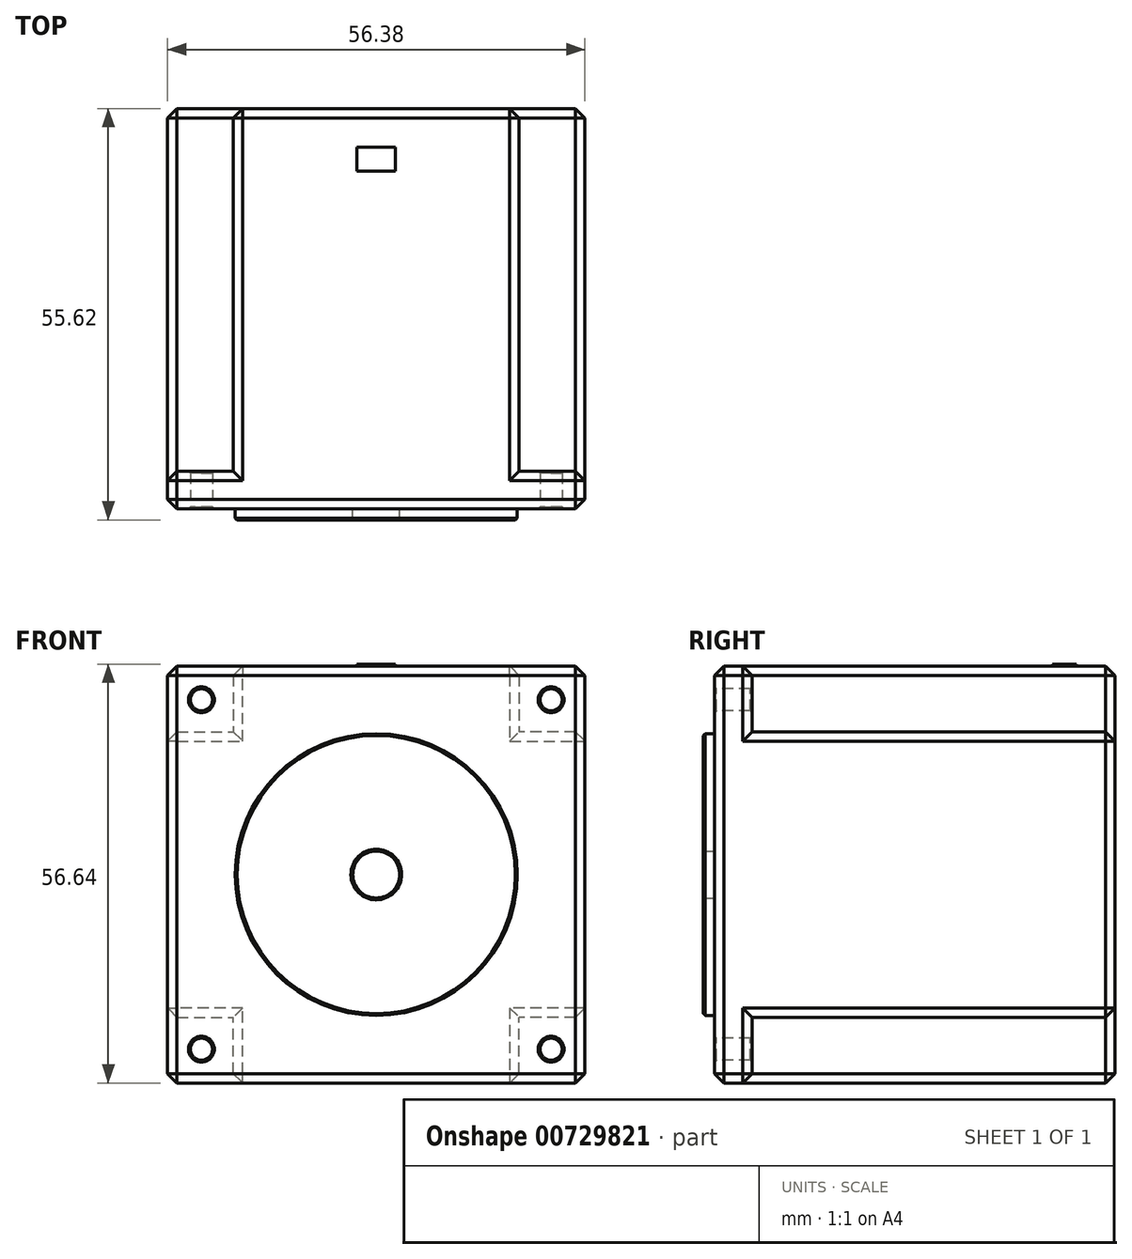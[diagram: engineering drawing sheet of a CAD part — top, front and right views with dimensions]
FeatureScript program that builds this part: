
annotation { "Feature Type Name" : "Feature", "Feature Type Description" : "" }
export const myFeature = defineFeature(function(context is Context, id is Id, definition is map)
    precondition{}
    {
        {
            var Q0;
            Q0=qCreatedBy(makeId("Front.planeOp"),FACE);
            var sketch = newSketch(context, id + "F0", { "sketchPlane" : qUnion([Q0])});
            skCircle(sketch, "E0", {"center": v(0, 0) * mm, "radius": 19.05 * mm});
            skLineSegment(sketch, "E1.bottom", {"start": v(28.2, 28.2) * mm, "end": v(-28.2, 28.2) * mm});
            skLineSegment(sketch, "E1.top", {"start": v(28.2, -28.2) * mm, "end": v(-28.2, -28.2) * mm});
            skLineSegment(sketch, "E1.left", {"start": v(28.2, 28.2) * mm, "end": v(28.2, -28.2) * mm});
            skLineSegment(sketch, "E1.right", {"start": v(-28.2, 28.2) * mm, "end": v(-28.2, -28.2) * mm});
            skCircle(sketch, "E2", {"center": v(0, 0) * mm, "radius": 3.18 * mm});
            skCircle(sketch, "E3", {"center": v(-23.62, 23.62) * mm, "radius": 1.49 * mm});
            skCircle(sketch, "E4", {"center": v(23.62, 23.62) * mm, "radius": 1.49 * mm});
            skCircle(sketch, "E5", {"center": v(23.62, -23.62) * mm, "radius": 1.49 * mm});
            skCircle(sketch, "E6", {"center": v(-23.62, -23.62) * mm, "radius": 1.49 * mm});
            skLineSegment(sketch, "E7", {"start": v(-23.62, 23.62) * mm, "end": v(-23.62, 28.2) * mm, "construction": true});
            skLineSegment(sketch, "E8", {"start": v(-23.62, 28.2) * mm, "end": v(-23.62, 23.62) * mm, "construction": true});
            skLineSegment(sketch, "E9", {"start": v(-23.62, 23.62) * mm, "end": v(-28.2, 23.62) * mm, "construction": true});
            skLineSegment(sketch, "E10", {"start": v(23.62, 23.62) * mm, "end": v(23.62, 28.2) * mm, "construction": true});
            skLineSegment(sketch, "E11", {"start": v(23.62, 23.62) * mm, "end": v(28.2, 23.62) * mm, "construction": true});
            skLineSegment(sketch, "E12", {"start": v(23.62, -23.62) * mm, "end": v(28.2, -23.62) * mm, "construction": true});
            skLineSegment(sketch, "E13", {"start": v(23.62, -23.62) * mm, "end": v(23.62, -28.2) * mm, "construction": true});
            skLineSegment(sketch, "E14", {"start": v(-23.62, -23.62) * mm, "end": v(-23.62, -28.2) * mm, "construction": true});
            skLineSegment(sketch, "E15", {"start": v(-23.62, -23.62) * mm, "end": v(-28.2, -23.62) * mm, "construction": true});
            skSolve(sketch);
        }
        {
            var Q0;
            Q0=qSketchRegion(id+"F0",true);
            var Q1;
            Q1=makeQuery(id+"F0.imprint","IMPRINT",FACE,{"disambiguationData":[TD([[makeQuery(id+"F0.imprint","IMPRINT",EDGE,{"derivedFrom":sQuery(id+"F0.wireOp",EDGE,"E0")}),1.0]])]});
            var Q2;
            Q2=makeQuery(id+"F0.imprint","IMPRINT",FACE,{"disambiguationData":[TD([[makeQuery(id+"F0.imprint","IMPRINT",EDGE,{"derivedFrom":sQuery(id+"F0.wireOp",EDGE,"E2")}),1.0]])]});
            extrude(context, id + "F1", {"entities" : qUnion([Q0, Q1, Q2]), "oppositeDirection" : true, "depth" : 54.1 * mm});
        }
        {
            var Q0;
            Q0=makeQuery(id+"F0.imprint","IMPRINT",FACE,{"disambiguationData":[TD([[makeQuery(id+"F0.imprint","IMPRINT",EDGE,{"derivedFrom":sQuery(id+"F0.wireOp",EDGE,"E0")}),1.0]])]});
            extrude(context, id + "F2", {"entities" : qUnion([Q0]), "operationType" : NewBodyOperationType.ADD, "depth" : 1.52 * mm});
        }
        {
            var Q0;
            Q0=makeQuery(id+"F0.imprint","IMPRINT",FACE,{"disambiguationData":[TD([[makeQuery(id+"F0.imprint","IMPRINT",EDGE,{"derivedFrom":sQuery(id+"F0.wireOp",EDGE,"E2")}),1.0]])]});
            extrude(context, id + "F3", {"entities" : qUnion([Q0]), "depth" : 20.32 * mm});
        }
        {
            var Q0;
            Q0=makeQuery(id+"F3.opExtrude","CAP_FACE",FACE,{"disambiguationData":[OSD([sQuery(id+"F0.wireOp",EDGE,"E2")])],"isStart":false});
            var sketch = newSketch(context, id + "F4", { "sketchPlane" : qUnion([Q0])});
            skLineSegment(sketch, "E16", {"start": v(-1.8, 2.62) * mm, "end": v(1.8, 2.62) * mm});
            skSolve(sketch);
        }
        {
            var Q0;
            {var subQ0=sQuery(id+"F4.wireOp",EDGE,"E16");Q0=makeQuery(id+"F4.imprint","IMPRINT",FACE,{"disambiguationData":[TD([[makeQuery(id+"F4.imprint","IMPRINT",EDGE,{"derivedFrom":subQ0}),1.0]])]});}
            extrude(context, id + "F5", {"entities" : qUnion([Q0]), "operationType" : NewBodyOperationType.REMOVE, "oppositeDirection" : true, "depth" : 12.7 * mm});
        }
        {
            var Q0;
            Q0=makeQuery(id+"F1.opExtrude","CAP_FACE",FACE,{"disambiguationData":[OSD([sQuery(id+"F0.wireOp",EDGE,"E1.bottom"),sQuery(id+"F0.wireOp",EDGE,"E1.top"),sQuery(id+"F0.wireOp",EDGE,"E1.left"),sQuery(id+"F0.wireOp",EDGE,"E1.right"),sQuery(id+"F0.wireOp",EDGE,"E3"),sQuery(id+"F0.wireOp",EDGE,"E4"),sQuery(id+"F0.wireOp",EDGE,"E5"),sQuery(id+"F0.wireOp",EDGE,"E6")])],"isStart":false});
            var sketch = newSketch(context, id + "F6", { "sketchPlane" : qUnion([Q0])});
            skLineSegment(sketch, "E17.bottom", {"start": v(-28.2, 28.2) * mm, "end": v(-19.3, 28.2) * mm});
            skLineSegment(sketch, "E17.top", {"start": v(-28.2, 19.3) * mm, "end": v(-19.3, 19.3) * mm});
            skLineSegment(sketch, "E17.left", {"start": v(-28.2, 28.2) * mm, "end": v(-28.2, 19.3) * mm});
            skLineSegment(sketch, "E17.right", {"start": v(-19.3, 28.2) * mm, "end": v(-19.3, 19.3) * mm});
            skLineSegment(sketch, "E18.bottom", {"start": v(28.2, 28.2) * mm, "end": v(19.3, 28.2) * mm});
            skLineSegment(sketch, "E18.top", {"start": v(28.2, 19.3) * mm, "end": v(19.3, 19.3) * mm});
            skLineSegment(sketch, "E18.left", {"start": v(28.2, 28.2) * mm, "end": v(28.2, 19.3) * mm});
            skLineSegment(sketch, "E18.right", {"start": v(19.3, 28.2) * mm, "end": v(19.3, 19.3) * mm});
            skLineSegment(sketch, "E19.bottom", {"start": v(28.2, -28.2) * mm, "end": v(19.3, -28.2) * mm});
            skLineSegment(sketch, "E19.top", {"start": v(28.2, -19.3) * mm, "end": v(19.3, -19.3) * mm});
            skLineSegment(sketch, "E19.left", {"start": v(28.2, -28.2) * mm, "end": v(28.2, -19.3) * mm});
            skLineSegment(sketch, "E19.right", {"start": v(19.3, -28.2) * mm, "end": v(19.3, -19.3) * mm});
            skLineSegment(sketch, "E20.bottom", {"start": v(-28.2, -28.2) * mm, "end": v(-19.3, -28.2) * mm});
            skLineSegment(sketch, "E20.top", {"start": v(-28.2, -19.3) * mm, "end": v(-19.3, -19.3) * mm});
            skLineSegment(sketch, "E20.left", {"start": v(-28.2, -28.2) * mm, "end": v(-28.2, -19.3) * mm});
            skLineSegment(sketch, "E20.right", {"start": v(-19.3, -28.2) * mm, "end": v(-19.3, -19.3) * mm});
            skSolve(sketch);
        }
        {
            var Q0;
            Q0=qSketchRegion(id+"F6",true);
            var Q1;
            {var subQ0=sQuery(id+"F0.wireOp",EDGE,"E1.right");var subQ1=sQuery(id+"F0.wireOp",EDGE,"E1.left");var subQ2=sQuery(id+"F0.wireOp",EDGE,"E1.top");var subQ3=sQuery(id+"F0.wireOp",EDGE,"E1.bottom");var subQ4=sQuery(id+"F0.wireOp",EDGE,"E3");var subQ5=sQuery(id+"F0.wireOp",EDGE,"E4");var subQ6=sQuery(id+"F0.wireOp",EDGE,"E5");var subQ7=sQuery(id+"F0.wireOp",EDGE,"E6");Q1=makeQuery(id+"F2.boolean.opBoolean","SPLIT",FACE,{"disambiguationData":[TD([makeQuery(id+"F1.opExtrude","SWEPT_FACE",FACE,{"disambiguationData":[OSD([subQ3])]})])],"derivedFrom":makeQuery(id+"F1.opExtrude","CAP_FACE",FACE,{"disambiguationData":[OSD([subQ3,subQ2,subQ1,subQ0,subQ4,subQ5,subQ6,subQ7])],"isStart":true})});}
            extrude(context, id + "F7", {"entities" : qUnion([Q0]), "operationType" : NewBodyOperationType.REMOVE, "oppositeDirection" : true, "endBoundEntityFace" : qUnion([Q1]), "depth" : 49.02 * mm});
        }
        {
            var Q0;
            Q0=makeQuery(id+"F1.opExtrude","SWEPT_FACE",FACE,{"disambiguationData":[OSD([sQuery(id+"F0.wireOp",EDGE,"E1.right")])]});
            var Q1;
            Q1=makeQuery(id+"F1.opExtrude","SWEPT_FACE",FACE,{"disambiguationData":[OSD([sQuery(id+"F0.wireOp",EDGE,"E1.bottom")])]});
            var Q2;
            Q2=makeQuery(id+"F1.opExtrude","SWEPT_FACE",FACE,{"disambiguationData":[OSD([sQuery(id+"F0.wireOp",EDGE,"E1.left")])]});
            var Q3;
            Q3=makeQuery(id+"F1.opExtrude","SWEPT_FACE",FACE,{"disambiguationData":[OSD([sQuery(id+"F0.wireOp",EDGE,"E1.top")])]});
            var Q4;
            Q4=makeQuery(id+"F1.opExtrude","CAP_FACE",FACE,{"disambiguationData":[OSD([sQuery(id+"F0.wireOp",EDGE,"E1.bottom"),sQuery(id+"F0.wireOp",EDGE,"E1.top"),sQuery(id+"F0.wireOp",EDGE,"E1.left"),sQuery(id+"F0.wireOp",EDGE,"E1.right"),sQuery(id+"F0.wireOp",EDGE,"E3"),sQuery(id+"F0.wireOp",EDGE,"E4"),sQuery(id+"F0.wireOp",EDGE,"E5"),sQuery(id+"F0.wireOp",EDGE,"E6")])],"isStart":false});
            chamfer(context, id + "F8", {"entities" : qUnion([Q0, Q1, Q2, Q3, Q4]), "width" : 1.27 * mm, "tangentPropagation" : true});
        }
        {
            var Q0;
            Q0=makeQuery(id+"F7.boolean.opBoolean","INTERSECT",EDGE,{"derivedFrom":[makeQuery(id+"F1.opExtrude","SWEPT_FACE",FACE,{"disambiguationData":[OSD([sQuery(id+"F0.wireOp",EDGE,"E3")])]}),makeQuery(id+"F7.opExtrude","CAP_FACE",FACE,{"disambiguationData":[OSD([sQuery(id+"F6.wireOp",EDGE,"E18.bottom"),sQuery(id+"F6.wireOp",EDGE,"E18.top"),sQuery(id+"F6.wireOp",EDGE,"E18.left"),sQuery(id+"F6.wireOp",EDGE,"E18.right")])],"isStart":false})]});
            var Q1;
            Q1=makeQuery(id+"F7.boolean.opBoolean","INTERSECT",EDGE,{"derivedFrom":[makeQuery(id+"F1.opExtrude","SWEPT_FACE",FACE,{"disambiguationData":[OSD([sQuery(id+"F0.wireOp",EDGE,"E6")])]}),makeQuery(id+"F7.opExtrude","CAP_FACE",FACE,{"disambiguationData":[OSD([sQuery(id+"F6.wireOp",EDGE,"E19.bottom"),sQuery(id+"F6.wireOp",EDGE,"E19.top"),sQuery(id+"F6.wireOp",EDGE,"E19.left"),sQuery(id+"F6.wireOp",EDGE,"E19.right")])],"isStart":false})]});
            var Q2;
            Q2=makeQuery(id+"F7.boolean.opBoolean","INTERSECT",EDGE,{"derivedFrom":[makeQuery(id+"F1.opExtrude","SWEPT_FACE",FACE,{"disambiguationData":[OSD([sQuery(id+"F0.wireOp",EDGE,"E4")])]}),makeQuery(id+"F7.opExtrude","CAP_FACE",FACE,{"disambiguationData":[OSD([sQuery(id+"F6.wireOp",EDGE,"E17.bottom"),sQuery(id+"F6.wireOp",EDGE,"E17.top"),sQuery(id+"F6.wireOp",EDGE,"E17.left"),sQuery(id+"F6.wireOp",EDGE,"E17.right")])],"isStart":false})]});
            var Q3;
            Q3=makeQuery(id+"F7.boolean.opBoolean","INTERSECT",EDGE,{"derivedFrom":[makeQuery(id+"F1.opExtrude","SWEPT_FACE",FACE,{"disambiguationData":[OSD([sQuery(id+"F0.wireOp",EDGE,"E5")])]}),makeQuery(id+"F7.opExtrude","CAP_FACE",FACE,{"disambiguationData":[OSD([sQuery(id+"F6.wireOp",EDGE,"E20.bottom"),sQuery(id+"F6.wireOp",EDGE,"E20.top"),sQuery(id+"F6.wireOp",EDGE,"E20.left"),sQuery(id+"F6.wireOp",EDGE,"E20.right")])],"isStart":false})]});
            var Q4;
            Q4=makeQuery(id+"F1.opExtrude","CAP_EDGE",EDGE,{"disambiguationData":[OSD([sQuery(id+"F0.wireOp",EDGE,"E5")])],"isStart":true});
            var Q5;
            Q5=makeQuery(id+"F1.opExtrude","CAP_EDGE",EDGE,{"disambiguationData":[OSD([sQuery(id+"F0.wireOp",EDGE,"E4")])],"isStart":true});
            var Q6;
            Q6=makeQuery(id+"F1.opExtrude","CAP_EDGE",EDGE,{"disambiguationData":[OSD([sQuery(id+"F0.wireOp",EDGE,"E3")])],"isStart":true});
            var Q7;
            Q7=makeQuery(id+"F1.opExtrude","CAP_EDGE",EDGE,{"disambiguationData":[OSD([sQuery(id+"F0.wireOp",EDGE,"E6")])],"isStart":true});
            var Q8;
            Q8=makeQuery(id+"F2.opExtrude","CAP_EDGE",EDGE,{"disambiguationData":[OSD([sQuery(id+"F0.wireOp",EDGE,"E0")])],"isStart":true});
            var Q9;
            Q9=makeQuery(id+"F2.opExtrude","CAP_EDGE",EDGE,{"disambiguationData":[OSD([sQuery(id+"F0.wireOp",EDGE,"E0")])],"isStart":false});
            var Q10;
            Q10=makeQuery(id+"F3.opExtrude","CAP_EDGE",EDGE,{"disambiguationData":[OSD([sQuery(id+"F0.wireOp",EDGE,"E2")])],"isStart":false});
            var Q11;
            Q11=makeQuery(id+"F5.boolean.opBoolean","COPY",EDGE,{"derivedFrom":makeQuery(id+"F5.opExtrude","CAP_EDGE",EDGE,{"disambiguationData":[OSD([sQuery(id+"F4.wireOp",EDGE,"E16")])],"isStart":true})});
            var Q12;
            Q12=makeQuery(id+"F2.opExtrude","CAP_EDGE",EDGE,{"disambiguationData":[OSD([sQuery(id+"F0.wireOp",EDGE,"E2")])],"isStart":false});
            chamfer(context, id + "F9", {"entities" : qUnion([Q0, Q1, Q2, Q3, Q4, Q5, Q6, Q7, Q8, Q9, Q10, Q11, Q12]), "width" : 0.25 * mm, "tangentPropagation" : true});
        }
        {
            var Q0;
            Q0=makeQuery(id+"F1.opExtrude","SWEPT_FACE",FACE,{"disambiguationData":[OSD([sQuery(id+"F0.wireOp",EDGE,"E1.bottom")])]});
            var sketch = newSketch(context, id + "F10", { "sketchPlane" : qUnion([Q0])});
            skLineSegment(sketch, "E21.bottom", {"start": v(2.6, 48.9) * mm, "end": v(-2.6, 48.9) * mm});
            skLineSegment(sketch, "E21.top", {"start": v(2.6, 45.63) * mm, "end": v(-2.6, 45.63) * mm});
            skLineSegment(sketch, "E21.left", {"start": v(2.6, 48.9) * mm, "end": v(2.6, 45.63) * mm});
            skLineSegment(sketch, "E21.right", {"start": v(-2.6, 48.9) * mm, "end": v(-2.6, 45.63) * mm});
            skPoint(sketch, "E21.middle", {"position": v(0, 47.26) * mm});
            skSolve(sketch);
        }
        {
            var Q0;
            Q0=qSketchRegion(id+"F10",true);
            extrude(context, id + "F11", {"entities" : qUnion([Q0]), "operationType" : NewBodyOperationType.ADD, "depth" : 0.25 * mm});
        }
        {
            var Q0;
            Q0=makeQuery(id+"F3.opExtrude","SWEPT_BODY",BODY,{"disambiguationData":[OSD([sQuery(id+"F0.wireOp",EDGE,"E2")])]});
            deleteBodies(context, id + "F12", {"entities" : qUnion([Q0])});
        }
    });
